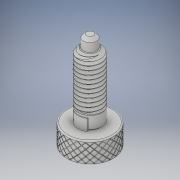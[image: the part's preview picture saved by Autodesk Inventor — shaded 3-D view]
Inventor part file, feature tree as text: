
AUTODESK INVENTOR PART (.ipt)
format: ipt  version: 2017.2 (Build 212233000, 233)  size: 1,973,760 bytes
history: native  units: in
note: dims shown in document units (in); Inventor stores cm internally (conversion verified against a paired STEP export)
features: chamfer x2, extrude x1, fillet x1, other x1
ambient origin geometry x8: Origin, YZ Plane, XZ Plane, XY Plane, X Axis, Y Axis, Z Axis, Center Point
bodies: Solid1 (feature_tree), Solid2 (feature_tree), Solid3 (feature_tree), Solid4 (feature_tree), Solid5 (feature_tree)
feature tree (5):
  chamfer  "Chamfer1"  [1 undecoded]
  extrude  "Extrude8"  [1 undecoded]
  fillet  "Fillet1"  [1 undecoded]
  chamfer  "Chamfer2"  [1 undecoded]
  other  "Cut-Extrude-Thin1[2]"
note: 4 required parameter values undecoded (feature->parameter linkage not recoverable at this tier; creation-order binding heuristic only, values carry confidence <= 0.55)
